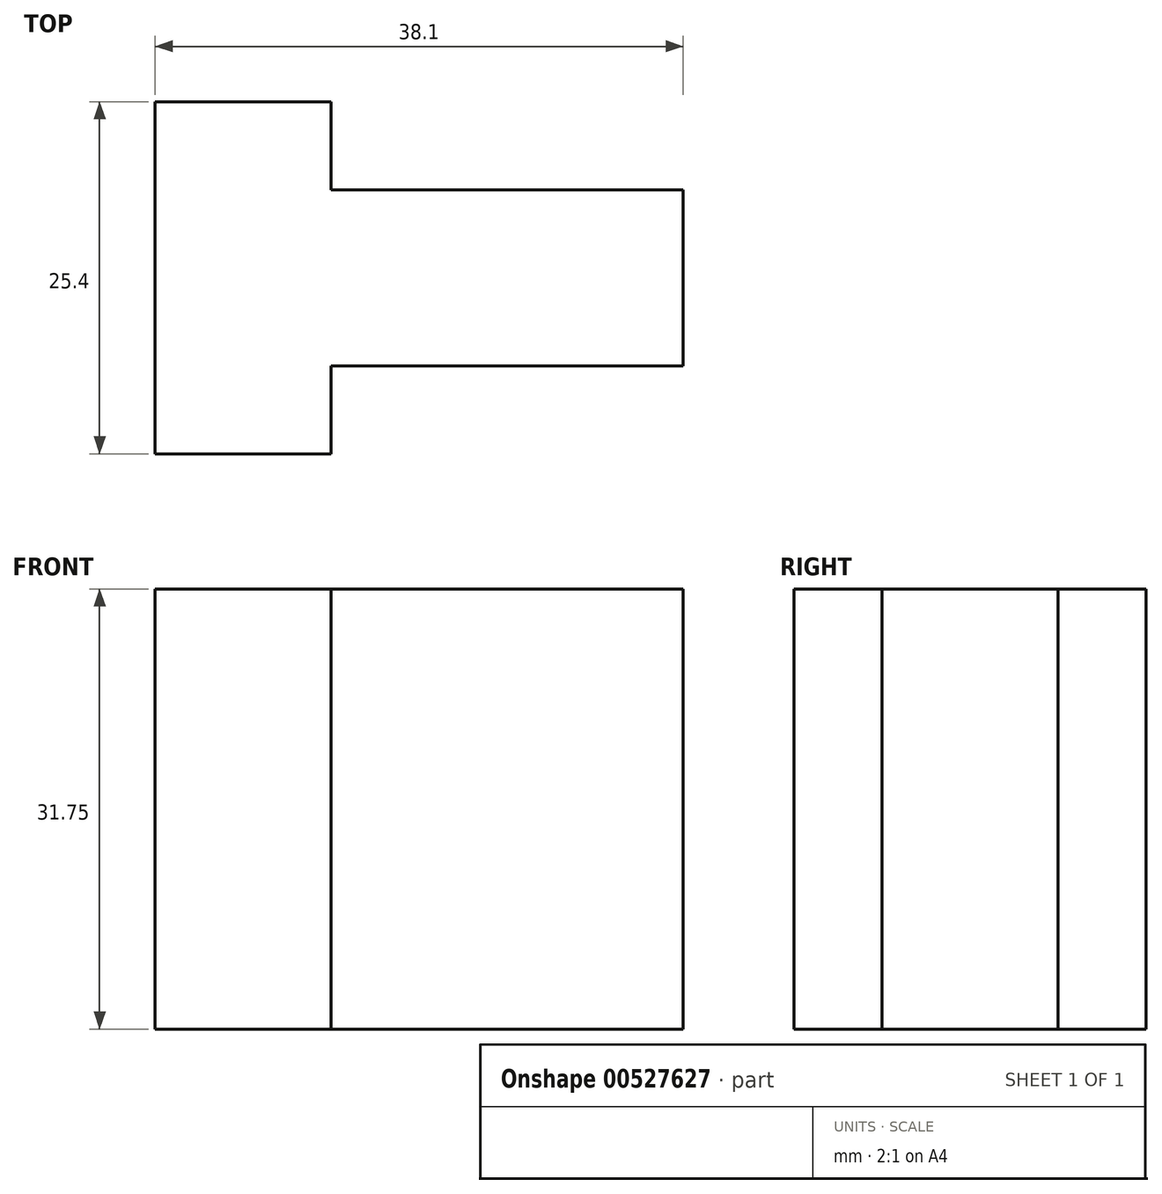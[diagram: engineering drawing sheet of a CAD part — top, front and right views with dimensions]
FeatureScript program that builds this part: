
annotation { "Feature Type Name" : "Feature", "Feature Type Description" : "" }
export const myFeature = defineFeature(function(context is Context, id is Id, definition is map)
    precondition{}
    {
        {
            var Q0;
            Q0=qCreatedBy(makeId("Top.planeOp"),FACE);
            var sketch = newSketch(context, id + "F0", { "sketchPlane" : qUnion([Q0])});
            skLineSegment(sketch, "E0", {"start": v(0, 0) * mm, "end": v(12.7, 0) * mm});
            skLineSegment(sketch, "E1", {"start": v(12.7, 0) * mm, "end": v(12.7, 6.35) * mm});
            skLineSegment(sketch, "E2", {"start": v(12.7, 6.35) * mm, "end": v(38.1, 6.35) * mm});
            skLineSegment(sketch, "E3", {"start": v(38.1, 6.35) * mm, "end": v(38.1, 19.05) * mm});
            skLineSegment(sketch, "E4", {"start": v(38.1, 19.05) * mm, "end": v(12.7, 19.05) * mm});
            skLineSegment(sketch, "E5", {"start": v(12.7, 19.05) * mm, "end": v(12.7, 25.4) * mm});
            skLineSegment(sketch, "E6", {"start": v(12.7, 25.4) * mm, "end": v(0, 25.4) * mm});
            skLineSegment(sketch, "E7", {"start": v(0, 25.4) * mm, "end": v(0, 0) * mm});
            skSolve(sketch);
        }
        {
            var Q0;
            Q0 = qSketchRegion(id + "F0", true);
            extrude(context, id + "F1", {"entities" : qUnion([Q0]), "depth" : 31.75 * mm, "offsetDistance" : 25.4 * mm});
        }
    });
